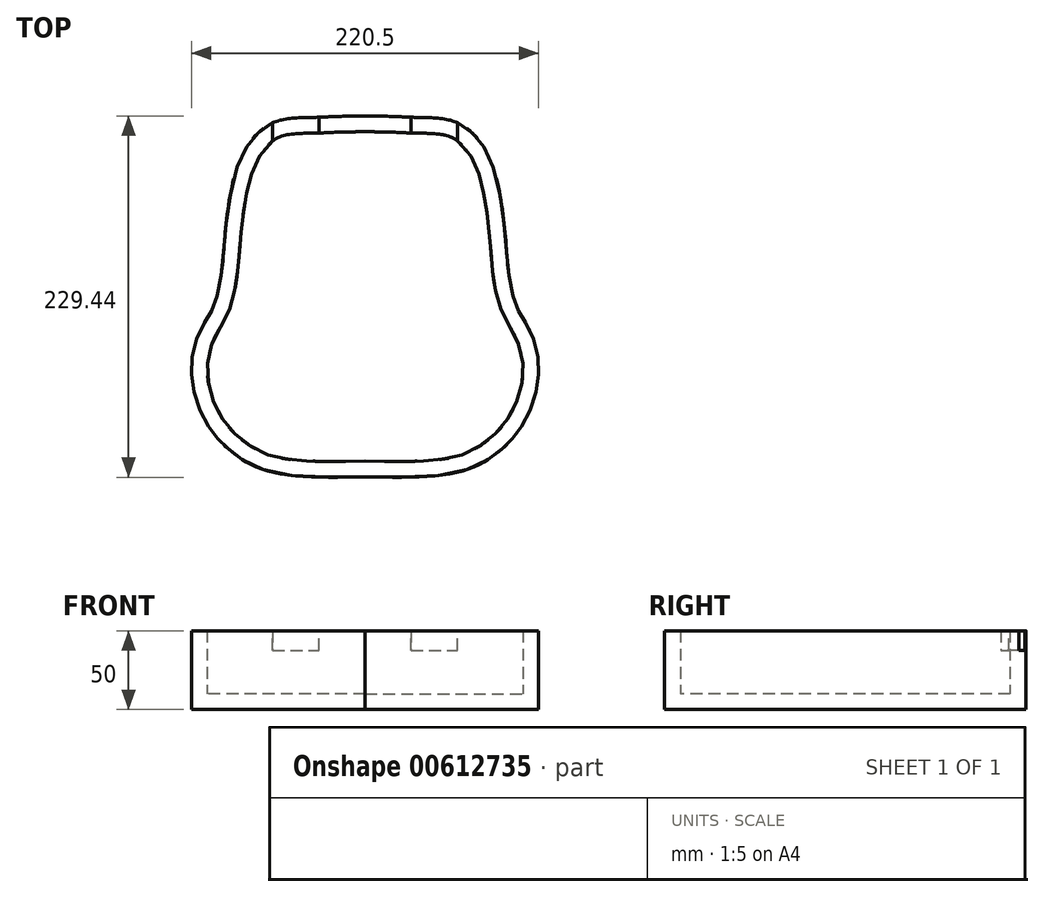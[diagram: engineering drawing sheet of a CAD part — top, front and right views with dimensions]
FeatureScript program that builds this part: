
annotation { "Feature Type Name" : "Feature", "Feature Type Description" : "" }
export const myFeature = defineFeature(function(context is Context, id is Id, definition is map)
    precondition{}
    {
        {
            var Q0;
            Q0=qCreatedBy(makeId("Top.planeOp"),FACE);
            var sketch = newSketch(context, id + "F0", { "sketchPlane" : qUnion([Q0])});
            skFitSpline(sketch, "E0", {"points": [v(0, 92.46) * mm, v(-30.72, 91.65) * mm, v(-55.15, 89.5) * mm, v(-69.4, 80.32) * mm, v(-80.35, 62.73) * mm, v(-88.63, 20.7) * mm, v(-91.91, -12.57) * mm, v(-96.74, -29.65) * mm, v(-101.1, -37.39) * mm, v(-108.33, -53.21) * mm, v(-110.21, -69.64) * mm, v(-107.64, -86.59) * mm, v(-100.19, -103.36) * mm, v(-92.8, -113.3) * mm, v(-84.5, -120.96) * mm, v(-62.4, -132.93) * mm, v(0, -136.8) * mm], "startDerivative": vector(-744.36, 0) * mm, "endDerivative": vector(685.33, 9.02) * mm});
            skFitSpline(sketch, "E1.MirrorCS", {"points": [v(0, 92.46) * mm, v(30.72, 91.65) * mm, v(55.15, 89.5) * mm, v(69.4, 80.32) * mm, v(80.35, 62.73) * mm, v(88.63, 20.7) * mm, v(91.91, -12.57) * mm, v(96.74, -29.65) * mm, v(101.1, -37.39) * mm, v(108.33, -53.21) * mm, v(110.21, -69.64) * mm, v(107.64, -86.59) * mm, v(100.19, -103.36) * mm, v(92.8, -113.3) * mm, v(84.5, -120.96) * mm, v(62.4, -132.93) * mm, v(0, -136.8) * mm], "startDerivative": vector(744.36, 0) * mm, "endDerivative": vector(-685.33, 9.02) * mm});
            skSolve(sketch);
        }
        {
            var Q0;
            Q0=makeQuery(id+"F0.imprint","IMPRINT",FACE,{"disambiguationData":[TD([[makeQuery(id+"F0.imprint","IMPRINT",EDGE,{"derivedFrom":sQuery(id+"F0.wireOp",EDGE,"E0")}),1.0]])]});
            extrude(context, id + "F1", {"entities" : qUnion([Q0]), "depth" : 50 * mm, "offsetDistance" : 25.4 * mm});
        }
        {
            var Q0;
            Q0=makeQuery(id+"F1.opExtrude","CAP_FACE",FACE,{"disambiguationData":[OSD([sQuery(id+"F0.wireOp",EDGE,"E0"),sQuery(id+"F0.wireOp",EDGE,"E1.MirrorCS")])],"isStart":false});
            shell(context, id + "F2", {"entities" : qUnion([Q0]), "thickness" : 10 * mm});
        }
        {
            var Q0;
            Q0=makeQuery(id+"F1.opExtrude","CAP_FACE",FACE,{"disambiguationData":[OSD([sQuery(id+"F0.wireOp",EDGE,"E0"),sQuery(id+"F0.wireOp",EDGE,"E1.MirrorCS")])],"isStart":false});
            var sketch = newSketch(context, id + "F3", { "sketchPlane" : qUnion([Q0])});
            skLineSegment(sketch, "E2", {"start": v(-58.8, 88.17) * mm, "end": v(-58.8, 76.53) * mm});
            skLineSegment(sketch, "E3", {"start": v(-29.19, 91.7) * mm, "end": v(-29.19, 81.7) * mm});
            skLineSegment(sketch, "E4.MirrorCS", {"start": v(58.8, 88.17) * mm, "end": v(58.8, 76.53) * mm});
            skLineSegment(sketch, "E5.MirrorCS", {"start": v(29.19, 91.7) * mm, "end": v(29.19, 81.7) * mm});
            skSolve(sketch);
        }
        {
            var Q0;
            {var subQ0=sQuery(id+"F3.wireOp",EDGE,"E2");Q0=makeQuery(id+"F3.imprint","IMPRINT",FACE,{"disambiguationData":[TD([[makeQuery(id+"F3.imprint","IMPRINT",EDGE,{"derivedFrom":subQ0}),1.0]])]});}
            extrude(context, id + "F4", {"entities" : qUnion([Q0]), "operationType" : NewBodyOperationType.REMOVE, "endBound" : BoundingType.SYMMETRIC, "oppositeDirection" : true, "depth" : 25 * mm, "offsetDistance" : 25 * mm});
        }
        {
            var Q0;
            {var subQ0=sQuery(id+"F3.wireOp",EDGE,"E4.MirrorCS");Q0=makeQuery(id+"F3.imprint","IMPRINT",FACE,{"disambiguationData":[TD([[makeQuery(id+"F3.imprint","IMPRINT",EDGE,{"derivedFrom":subQ0}),-1.0]])]});}
            extrude(context, id + "F5", {"entities" : qUnion([Q0]), "operationType" : NewBodyOperationType.REMOVE, "endBound" : BoundingType.SYMMETRIC, "oppositeDirection" : true, "depth" : 25 * mm, "offsetDistance" : 25 * mm});
        }
    });
